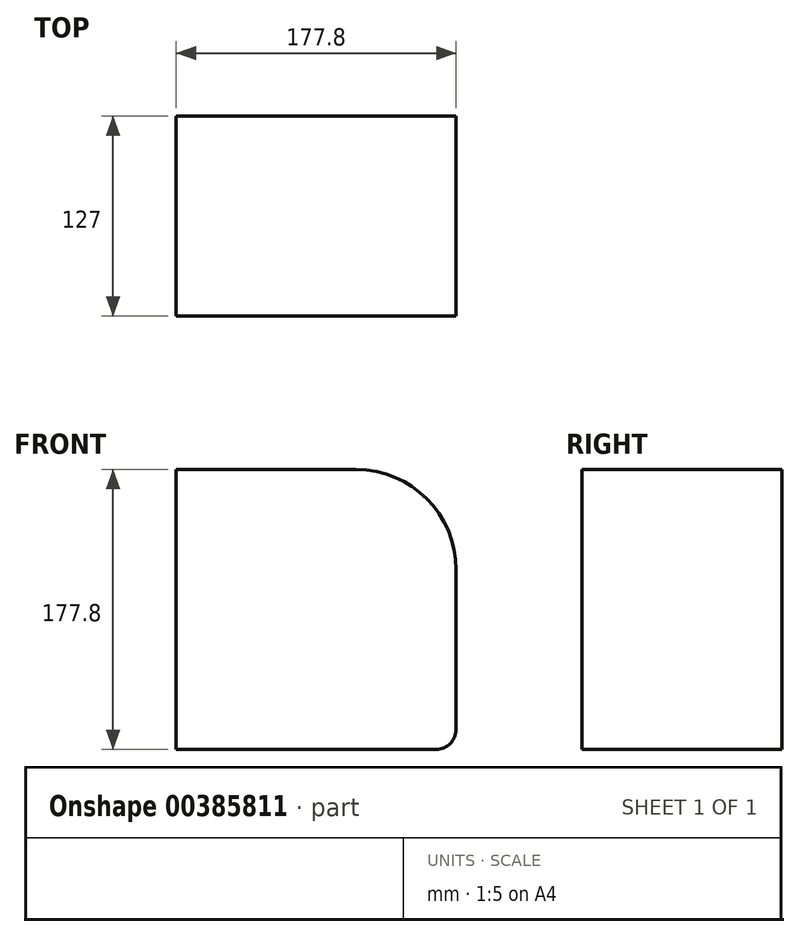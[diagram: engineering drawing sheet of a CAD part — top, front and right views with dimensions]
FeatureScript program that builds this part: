
annotation { "Feature Type Name" : "Feature", "Feature Type Description" : "" }
export const myFeature = defineFeature(function(context is Context, id is Id, definition is map)
    precondition{}
    {
        {
            var Q0;
            Q0=qCreatedBy(makeId("Front.planeOp"),FACE);
            var sketch = newSketch(context, id + "F0", { "sketchPlane" : qUnion([Q0])});
            skLineSegment(sketch, "E0.bottom", {"start": v(-177.8, 177.8) * mm, "end": v(-63.5, 177.8) * mm});
            skLineSegment(sketch, "E0.top", {"start": v(-177.8, 0) * mm, "end": v(0, 0) * mm});
            skLineSegment(sketch, "E0.left", {"start": v(-177.8, 177.8) * mm, "end": v(-177.8, 0) * mm});
            skLineSegment(sketch, "E0.right", {"start": v(0, 114.3) * mm, "end": v(0, 0) * mm});
            skArc(sketch, "E1", {"start": v(0, 114.3) * mm, "mid": v(-18.6, 159.2) * mm, "end": v(-63.5, 177.8) * mm});
            skSolve(sketch);
        }
        {
            var Q0;
            Q0=makeQuery(id+"F0.imprint","IMPRINT",FACE,{"disambiguationData":[TD([[makeQuery(id+"F0.imprint","IMPRINT",EDGE,{"derivedFrom":sQuery(id+"F0.wireOp",EDGE,"E0.bottom")}),-1.0]])]});
            extrude(context, id + "F1", {"entities" : qUnion([Q0]), "oppositeDirection" : true, "depth" : 127 * mm});
        }
        {
            var Q0;
            Q0=makeQuery(id+"F1.opExtrude","SWEPT_EDGE",EDGE,{"disambiguationData":[OSD([sQuery(id+"F0.wireOp",EDGE,"E0.top"),sQuery(id+"F0.wireOp",EDGE,"E0.right")])]});
            fillet(context, id + "F2", {"entities" : qUnion([Q0]), "radius" : 12.7 * mm, "tangentPropagation" : true, "allowEdgeOverflow" : false});
        }
    });
